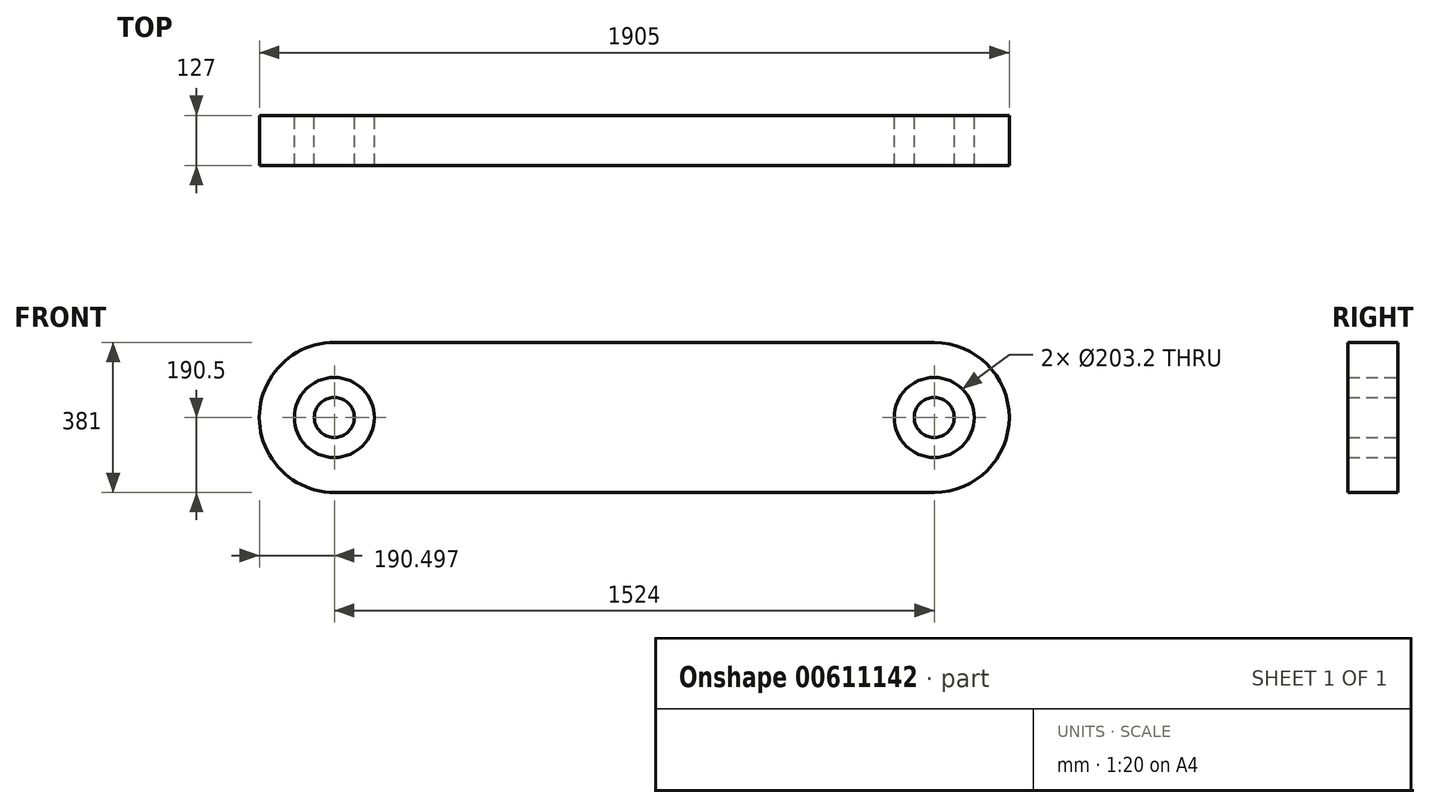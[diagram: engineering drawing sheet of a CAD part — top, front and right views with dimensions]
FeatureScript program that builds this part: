
annotation { "Feature Type Name" : "Feature", "Feature Type Description" : "" }
export const myFeature = defineFeature(function(context is Context, id is Id, definition is map)
    precondition{}
    {
        {
            var Q0;
            Q0=qCreatedBy(makeId("Front.planeOp"),FACE);
            var sketch = newSketch(context, id + "F0", { "sketchPlane" : qUnion([Q0])});
            skLineSegment(sketch, "E0.bottom", {"start": v(762, 190.5) * mm, "end": v(-762, 190.5) * mm});
            skLineSegment(sketch, "E0.top", {"start": v(762, -190.5) * mm, "end": v(-762, -190.5) * mm});
            skPoint(sketch, "E0.middle", {"position": v(0, 0) * mm});
            skArc(sketch, "E1", {"start": v(-762, 190.5) * mm, "mid": v(-952.5, 0) * mm, "end": v(-762, -190.5) * mm});
            skArc(sketch, "E2", {"start": v(762, -190.5) * mm, "mid": v(952.5, 0) * mm, "end": v(762, 190.5) * mm});
            skCircle(sketch, "E3", {"center": v(-762, 0) * mm, "radius": 101.6 * mm});
            skCircle(sketch, "E4", {"center": v(762, 0) * mm, "radius": 101.6 * mm});
            skCircle(sketch, "E5", {"center": v(-762, 0) * mm, "radius": 50.8 * mm});
            skCircle(sketch, "E6", {"center": v(762, 0) * mm, "radius": 50.8 * mm});
            skSolve(sketch);
        }
        {
            var Q0;
            Q0=makeQuery(id+"F0.imprint","IMPRINT",FACE,{"disambiguationData":[TD([[makeQuery(id+"F0.imprint","IMPRINT",EDGE,{"derivedFrom":sQuery(id+"F0.wireOp",EDGE,"E0.bottom")}),1.0]])]});
            var Q1;
            Q1=makeQuery(id+"F0.imprint","IMPRINT",FACE,{"disambiguationData":[TD([[makeQuery(id+"F0.imprint","IMPRINT",EDGE,{"derivedFrom":sQuery(id+"F0.wireOp",EDGE,"E5")}),1.0]])]});
            var Q2;
            Q2=makeQuery(id+"F0.imprint","IMPRINT",FACE,{"disambiguationData":[TD([[makeQuery(id+"F0.imprint","IMPRINT",EDGE,{"derivedFrom":sQuery(id+"F0.wireOp",EDGE,"E6")}),1.0]])]});
            extrude(context, id + "F1", {"entities" : qUnion([Q0, Q1, Q2]), "endBound" : BoundingType.SYMMETRIC, "depth" : 127 * mm, "offsetDistance" : 25.4 * mm});
        }
    });
